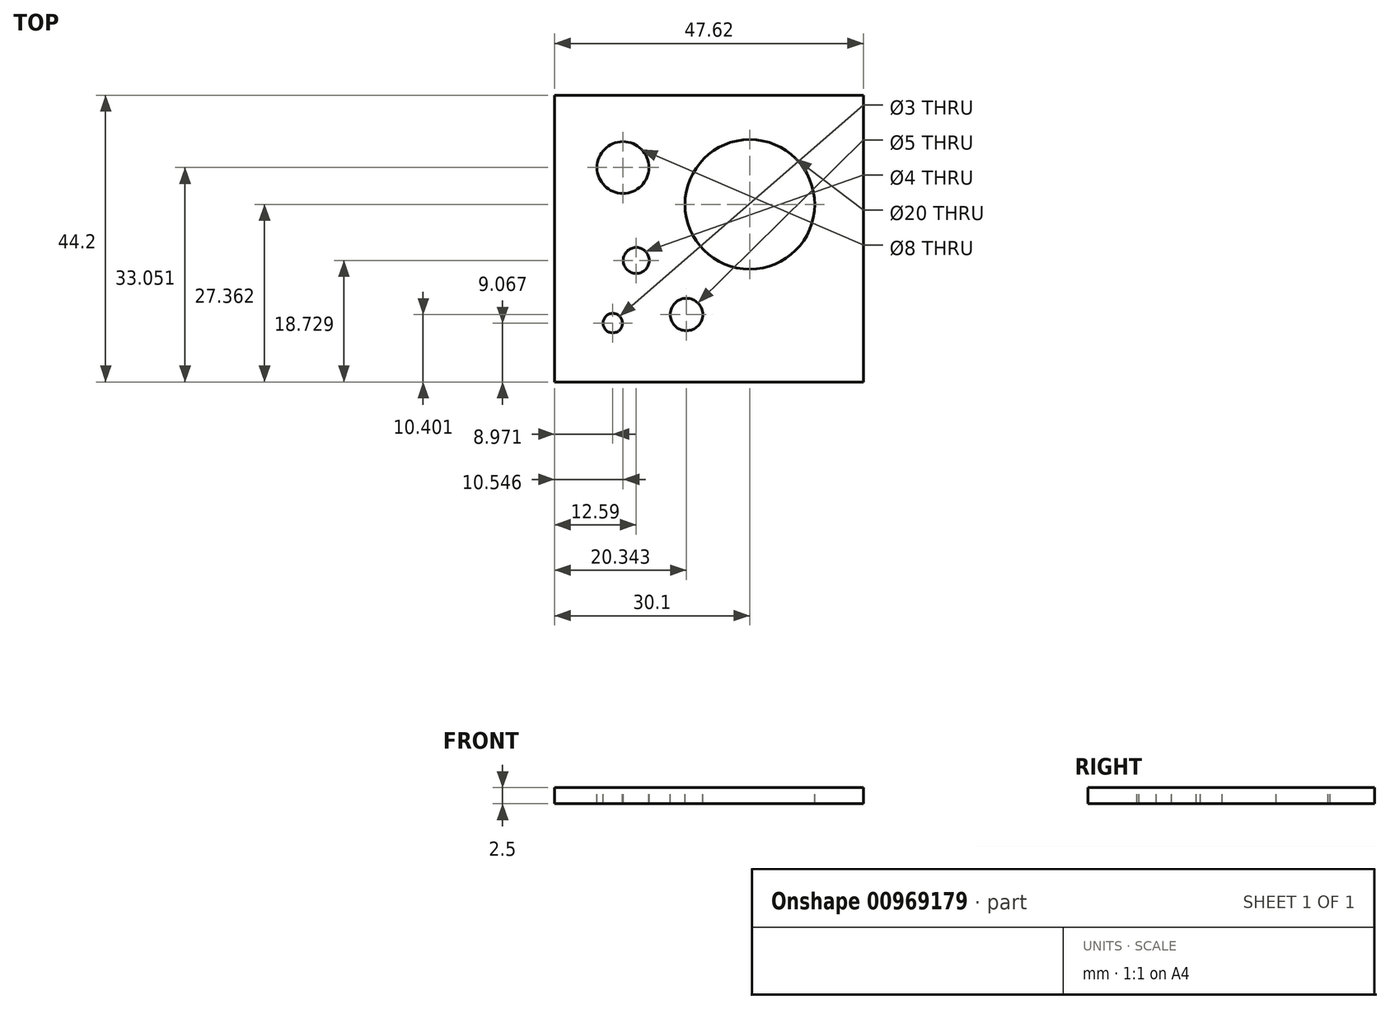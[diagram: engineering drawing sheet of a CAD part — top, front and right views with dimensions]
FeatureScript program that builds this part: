
annotation { "Feature Type Name" : "Feature", "Feature Type Description" : "" }
export const myFeature = defineFeature(function(context is Context, id is Id, definition is map)
    precondition{}
    {
        {
            var Q0;
            Q0=qCreatedBy(makeId("Top.planeOp"),FACE);
            var sketch = newSketch(context, id + "F0", { "sketchPlane" : qUnion([Q0])});
            skLineSegment(sketch, "E0.bottom", {"start": v(-37.47, 19.69) * mm, "end": v(10.15, 19.69) * mm});
            skLineSegment(sketch, "E0.top", {"start": v(-37.47, -24.51) * mm, "end": v(10.15, -24.51) * mm});
            skLineSegment(sketch, "E0.left", {"start": v(-37.47, 19.69) * mm, "end": v(-37.47, -24.51) * mm});
            skLineSegment(sketch, "E0.right", {"start": v(10.15, 19.69) * mm, "end": v(10.15, -24.51) * mm});
            skSolve(sketch);
        }
        {
            var Q0;
            Q0 = qSketchRegion(id + "F0", true);
            extrude(context, id + "F1", {"entities" : qUnion([Q0]), "depth" : 2.5 * mm, "offsetDistance" : 25 * mm});
        }
        {
            var Q0;
            Q0=makeQuery(id+"F1.opExtrude","CAP_FACE",FACE,{"disambiguationData":[OSD([sQuery(id+"F0.wireOp",EDGE,"E0.bottom"),sQuery(id+"F0.wireOp",EDGE,"E0.top"),sQuery(id+"F0.wireOp",EDGE,"E0.left"),sQuery(id+"F0.wireOp",EDGE,"E0.right")])],"isStart":false});
            var sketch = newSketch(context, id + "F2", { "sketchPlane" : qUnion([Q0])});
            skCircle(sketch, "E1", {"center": v(-28.5, -15.44) * mm, "radius": 1.5 * mm});
            skCircle(sketch, "E2", {"center": v(-26.92, 8.54) * mm, "radius": 4 * mm});
            skCircle(sketch, "E3", {"center": v(-7.37, 2.85) * mm, "radius": 10 * mm});
            skCircle(sketch, "E4", {"center": v(-24.88, -5.78) * mm, "radius": 2 * mm});
            skCircle(sketch, "E5", {"center": v(-17.13, -14.1) * mm, "radius": 2.5 * mm});
            skSolve(sketch);
        }
        {
            var Q0;
            Q0 = qSketchRegion(id + "F2", true);
            extrude(context, id + "F3", {"entities" : qUnion([Q0]), "operationType" : NewBodyOperationType.REMOVE, "oppositeDirection" : true, "depth" : 3 * mm, "offsetDistance" : 25 * mm});
        }
    });
